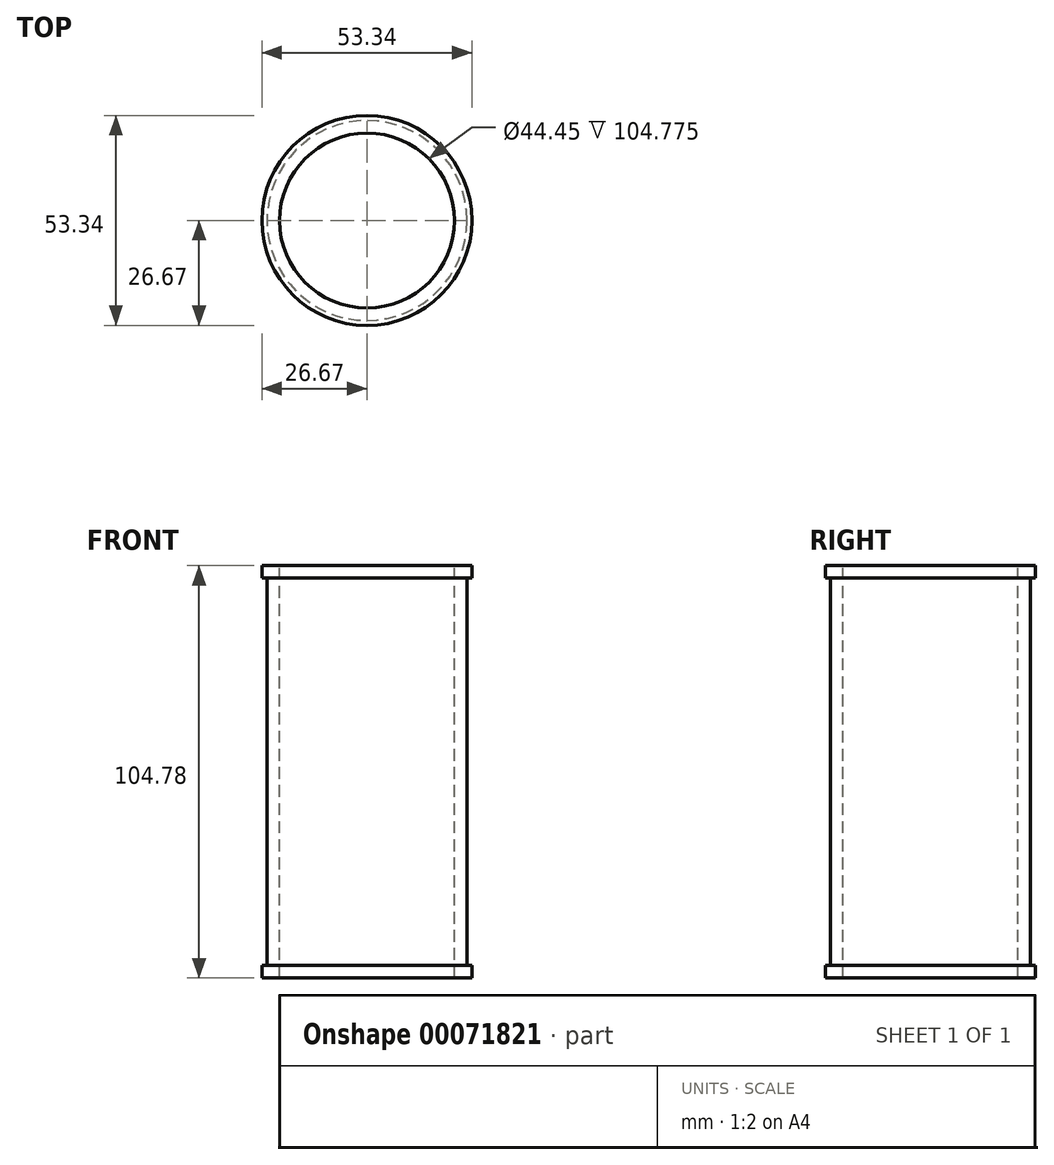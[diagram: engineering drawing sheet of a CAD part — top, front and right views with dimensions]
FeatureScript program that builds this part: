
annotation { "Feature Type Name" : "Feature", "Feature Type Description" : "" }
export const myFeature = defineFeature(function(context is Context, id is Id, definition is map)
    precondition{}
    {
        {
            var Q0;
            Q0=qCreatedBy(makeId("Top.planeOp"),FACE);
            var sketch = newSketch(context, id + "F0", { "sketchPlane" : qUnion([Q0])});
            skCircle(sketch, "E0", {"center": v(0, 0) * mm, "radius": 26.67 * mm});
            skSolve(sketch);
        }
        {
            var Q0;
            Q0 = qSketchRegion(id + "F0", true);
            extrude(context, id + "F1", {"entities" : qUnion([Q0]), "depth" : 3.17 * mm});
        }
        {
            var Q0;
            Q0=makeQuery(id+"F1.opExtrude","CAP_FACE",FACE,{"disambiguationData":[OSD([sQuery(id+"F0.wireOp",EDGE,"E0")])],"isStart":false});
            var sketch = newSketch(context, id + "F2", { "sketchPlane" : qUnion([Q0])});
            skCircle(sketch, "E1", {"center": v(0, 0) * mm, "radius": 25.4 * mm});
            skSolve(sketch);
        }
        {
            var Q0;
            Q0 = qSketchRegion(id + "F2", true);
            extrude(context, id + "F3", {"entities" : qUnion([Q0]), "operationType" : NewBodyOperationType.ADD, "depth" : 98.42 * mm});
        }
        {
            var Q0;
            Q0=makeQuery(id+"F3.opExtrude","CAP_FACE",FACE,{"disambiguationData":[OSD([sQuery(id+"F2.wireOp",EDGE,"E1")])],"isStart":false});
            var sketch = newSketch(context, id + "F4", { "sketchPlane" : qUnion([Q0])});
            skCircle(sketch, "E2", {"center": v(0, 0) * mm, "radius": 26.67 * mm});
            skSolve(sketch);
        }
        {
            var Q0;
            Q0 = qSketchRegion(id + "F4", true);
            extrude(context, id + "F5", {"entities" : qUnion([Q0]), "operationType" : NewBodyOperationType.ADD, "depth" : 3.17 * mm});
        }
        {
            var Q0;
            Q0=makeQuery(id+"F5.opExtrude","CAP_FACE",FACE,{"disambiguationData":[OSD([sQuery(id+"F4.wireOp",EDGE,"E2")])],"isStart":false});
            var sketch = newSketch(context, id + "F6", { "sketchPlane" : qUnion([Q0])});
            skCircle(sketch, "E3", {"center": v(0, 0) * mm, "radius": 22.23 * mm});
            skSolve(sketch);
        }
        {
            var Q0;
            Q0 = qSketchRegion(id + "F6", true);
            extrude(context, id + "F7", {"entities" : qUnion([Q0]), "operationType" : NewBodyOperationType.REMOVE, "oppositeDirection" : true, "depth" : 127 * mm});
        }
    });
